annotation { "Feature Type Name" : "Feature", "Feature Type Description" : "" }
export const myFeature = defineFeature(function(context is Context, id is Id, definition is map)
    precondition{}
    {
        {
            var Q0;
            Q0=qCreatedBy(makeId("Front.planeOp"),FACE);
            var sketch = newSketch(context, id + "F0", { "sketchPlane" : qUnion([Q0])});
            skLineSegment(sketch, "E0", {"start": v(-25, 0) * mm, "end": v(-25, -40) * mm});
            skLineSegment(sketch, "E1", {"start": v(25, 0) * mm, "end": v(25, -40) * mm});
            skArc(sketch, "E2", {"start": v(25, 0) * mm, "mid": v(0, 25) * mm, "end": v(-25, 0) * mm});
            skArc(sketch, "E3.0", {"start": v(15, 0) * mm, "mid": v(0, 15) * mm, "end": v(-15, 0) * mm});
            skLineSegment(sketch, "E4.0", {"start": v(-15, 0) * mm, "end": v(-15, -40) * mm});
            skLineSegment(sketch, "E5.0", {"start": v(15, 0) * mm, "end": v(15, -40) * mm});
            skLineSegment(sketch, "E6", {"start": v(-15, -40) * mm, "end": v(-25, -40) * mm});
            skLineSegment(sketch, "E7", {"start": v(15, -40) * mm, "end": v(25, -40) * mm});
            skSolve(sketch);
        }
        {
            var Q0;
            Q0=qCreatedBy(makeId("Right.planeOp"),FACE);
            var sketch = newSketch(context, id + "F1", { "sketchPlane" : qUnion([Q0])});
            skLineSegment(sketch, "E8.0", {"start": v(-15, -25) * mm, "end": v(-15, -40) * mm});
            skLineSegment(sketch, "E9.0", {"start": v(15, -25) * mm, "end": v(15, -40) * mm});
            skLineSegment(sketch, "E10.0", {"start": v(-15, -40) * mm, "end": v(15, -40) * mm});
            skArc(sketch, "E11", {"start": v(-15, -25) * mm, "mid": v(0, -40) * mm, "end": v(15, -25) * mm});
            skSolve(sketch);
        }
        {
            var Q0;
            Q0=qCreatedBy(makeId("Right.planeOp"),FACE);
            var sketch = newSketch(context, id + "F2", { "sketchPlane" : qUnion([Q0])});
            skCircle(sketch, "E12", {"center": v(0, -25) * mm, "radius": 6 * mm});
            skSolve(sketch);
        }
        {
            var Q0;
            Q0=qCreatedBy(makeId("Top.planeOp"),FACE);
            cPlane(context, id + "F3", {"entities" : qUnion([Q0]), "cplaneType" : CPlaneType.OFFSET, "offset" : 25 * mm, "width" : 150 * mm, "height" : 150 * mm});
        }
        {
            var Q0;
            Q0=makeQuery(id+"F0.imprint","IMPRINT",FACE,{"disambiguationData":[TD([[makeQuery(id+"F0.imprint","IMPRINT",EDGE,{"derivedFrom":sQuery(id+"F0.wireOp",EDGE,"E0")}),1.0]])]});
            extrude(context, id + "F4", {"entities" : qUnion([Q0]), "depth" : 30 * mm, "symmetric" : true});
        }
        {
            var Q0;
            Q0 = qSketchRegion(id + "F1", true);
            extrude(context, id + "F5", {"entities" : qUnion([Q0]), "operationType" : NewBodyOperationType.REMOVE, "oppositeDirection" : true, "depth" : 100 * mm, "symmetric" : true});
        }
        {
            var Q0;
            Q0 = qSketchRegion(id + "F2", true);
            extrude(context, id + "F6", {"entities" : qUnion([Q0]), "operationType" : NewBodyOperationType.REMOVE, "oppositeDirection" : true, "depth" : 100 * mm, "symmetric" : true});
        }
        {
            var Q0;
            Q0=qCreatedBy(id+"F3.planeOp",FACE);
            var sketch = newSketch(context, id + "F7", { "sketchPlane" : qUnion([Q0])});
            skArc(sketch, "E13", {"start": v(-10.34, 10.86) * mm, "mid": v(-12.7, 8) * mm, "end": v(-14.27, 4.64) * mm});
            skLineSegment(sketch, "E14", {"start": v(-10.34, 10.86) * mm, "end": v(-4.34, 10.86) * mm});
            skLineSegment(sketch, "E15", {"start": v(-4.34, 10.86) * mm, "end": v(0, 15) * mm});
            skLineSegment(sketch, "E16.1.0", {"start": v(-11.67, -0.78) * mm, "end": v(-14.27, 4.64) * mm});
            skLineSegment(sketch, "E16.1.1", {"start": v(-13.53, -6.48) * mm, "end": v(-11.67, -0.78) * mm});
            skLineSegment(sketch, "E16.2.0", {"start": v(-2.87, -11.34) * mm, "end": v(-8.82, -12.14) * mm});
            skLineSegment(sketch, "E16.2.1", {"start": v(1.98, -14.87) * mm, "end": v(-2.87, -11.34) * mm});
            skLineSegment(sketch, "E16.3.0", {"start": v(9.9, -6.23) * mm, "end": v(8.82, -12.14) * mm});
            skLineSegment(sketch, "E16.3.1", {"start": v(14.75, -2.7) * mm, "end": v(9.9, -6.23) * mm});
            skLineSegment(sketch, "E16.4.0", {"start": v(8.99, 7.49) * mm, "end": v(14.27, 4.64) * mm});
            skLineSegment(sketch, "E16.4.1", {"start": v(7.13, 13.2) * mm, "end": v(8.99, 7.49) * mm});
            skArc(sketch, "E17.trimOffspring", {"start": v(7.13, 13.2) * mm, "mid": v(3.68, 14.54) * mm, "end": v(0, 15) * mm});
            skArc(sketch, "E18.trimOffspring", {"start": v(14.75, -2.7) * mm, "mid": v(14.97, 1) * mm, "end": v(14.27, 4.64) * mm});
            skArc(sketch, "E19.trimOffspring", {"start": v(1.98, -14.87) * mm, "mid": v(5.57, -13.93) * mm, "end": v(8.82, -12.14) * mm});
            skArc(sketch, "E20.trimOffspring", {"start": v(-13.53, -6.48) * mm, "mid": v(-11.52, -9.6) * mm, "end": v(-8.82, -12.14) * mm});
            skSolve(sketch);
        }
        {
            var Q0;
            Q0 = qSketchRegion(id + "F7", true);
            var Q1;
            Q1=makeQuery(id+"F4.opExtrude","SWEPT_FACE",FACE,{"disambiguationData":[OSD([sQuery(id+"F0.wireOp",EDGE,"E2")])]});
            var Q2;
            Q2=makeQuery(id+"F4.opExtrude","SWEPT_BODY",BODY,{"disambiguationData":[OSD([sQuery(id+"F0.wireOp",EDGE,"E0"),sQuery(id+"F0.wireOp",EDGE,"E1"),sQuery(id+"F0.wireOp",EDGE,"E2"),sQuery(id+"F0.wireOp",EDGE,"E3.0"),sQuery(id+"F0.wireOp",EDGE,"E4.0"),sQuery(id+"F0.wireOp",EDGE,"E5.0"),sQuery(id+"F0.wireOp",EDGE,"E6"),sQuery(id+"F0.wireOp",EDGE,"E7")])]});
            extrude(context, id + "F8", {"entities" : qUnion([Q0]), "operationType" : NewBodyOperationType.ADD, "endBound" : BoundingType.UP_TO_SURFACE, "oppositeDirection" : true, "endBoundEntityFace" : qUnion([Q1]), "endBoundEntityBody" : qUnion([Q2]), "depth" : 25 * mm, "hasSecondDirection" : true, "secondDirectionOppositeDirection" : false, "secondDirectionDepth" : 15 * mm});
        }
        {
            var Q0;
            Q0=makeQuery(id+"F8.opExtrude","CAP_FACE",FACE,{"disambiguationData":[OSD([sQuery(id+"F7.wireOp",EDGE,"E13"),sQuery(id+"F7.wireOp",EDGE,"E14"),sQuery(id+"F7.wireOp",EDGE,"E15"),sQuery(id+"F7.wireOp",EDGE,"E16.1.0"),sQuery(id+"F7.wireOp",EDGE,"E16.1.1"),sQuery(id+"F7.wireOp",EDGE,"E16.2.0"),sQuery(id+"F7.wireOp",EDGE,"E16.2.1"),sQuery(id+"F7.wireOp",EDGE,"E16.3.0"),sQuery(id+"F7.wireOp",EDGE,"E16.3.1"),sQuery(id+"F7.wireOp",EDGE,"E16.4.0"),sQuery(id+"F7.wireOp",EDGE,"E16.4.1"),sQuery(id+"F7.wireOp",EDGE,"E17.trimOffspring"),sQuery(id+"F7.wireOp",EDGE,"E18.trimOffspring"),sQuery(id+"F7.wireOp",EDGE,"E19.trimOffspring"),sQuery(id+"F7.wireOp",EDGE,"E20.trimOffspring")])],"isStart":true});
            var sketch = newSketch(context, id + "F9", { "sketchPlane" : qUnion([Q0])});
            skCircle(sketch, "E21", {"center": v(0, 0) * mm, "radius": 6 * mm});
            skSolve(sketch);
        }
        {
            var Q0;
            Q0 = qSketchRegion(id + "F9", true);
            extrude(context, id + "F10", {"entities" : qUnion([Q0]), "operationType" : NewBodyOperationType.REMOVE, "oppositeDirection" : true, "depth" : 10 * mm});
        }
        {
            var Q0;
            Q0=makeQuery(id+"F4.opExtrude","SWEPT_FACE",FACE,{"disambiguationData":[OSD([sQuery(id+"F0.wireOp",EDGE,"E1")])]});
            var sketch = newSketch(context, id + "F11", { "sketchPlane" : qUnion([Q0])});
            skText(sketch, "E22", { "text": "PROUDLY NIGERIAN", "fontName": "DroidSansMono.ttf"});
            const initialGuessF11  = {"E22": [-0.013, -0.013, 1, 0, 0.00166]};
            skSetInitialGuess(sketch, initialGuessF11);
            skSolve(sketch);
        }
        {
            var Q0;
            Q0 = qSketchRegion(id + "F11", true);
            extrude(context, id + "F12", {"entities" : qUnion([Q0]), "operationType" : NewBodyOperationType.ADD, "depth" : 0.5 * mm});
        }
    });